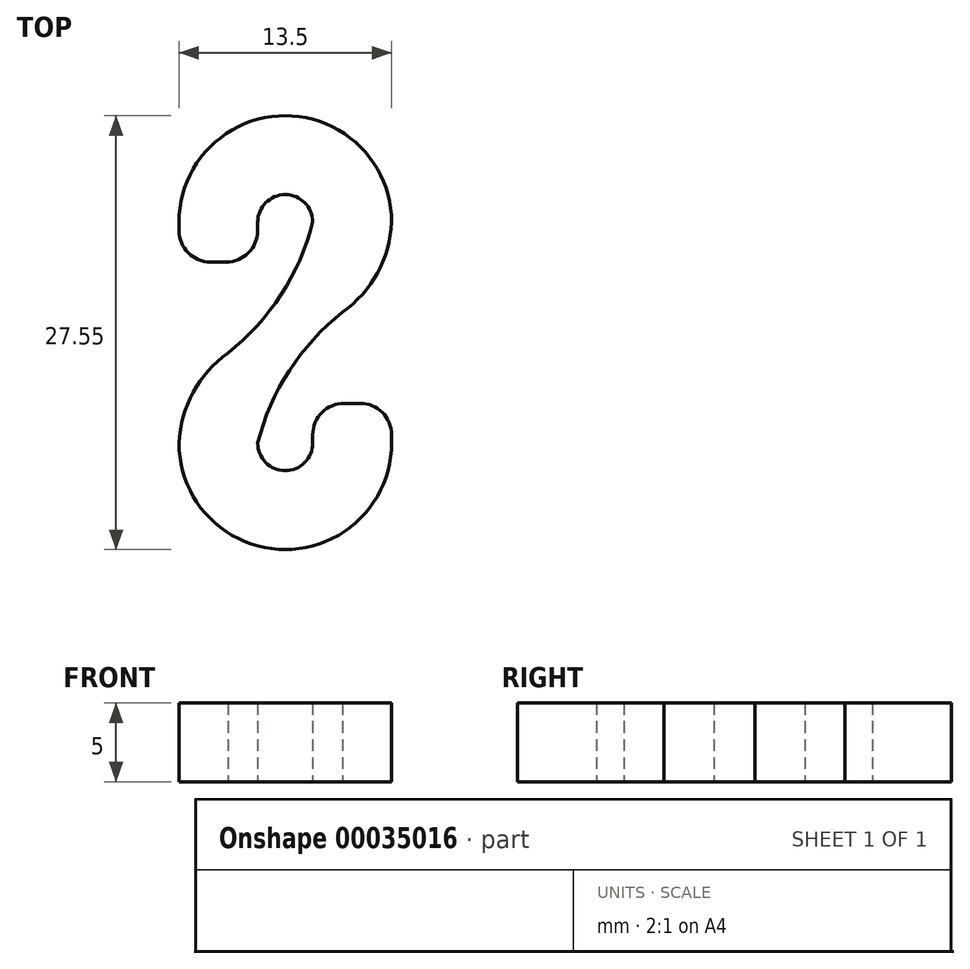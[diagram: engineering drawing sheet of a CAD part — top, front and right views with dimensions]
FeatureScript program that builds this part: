
annotation { "Feature Type Name" : "Feature", "Feature Type Description" : "" }
export const myFeature = defineFeature(function(context is Context, id is Id, definition is map)
    precondition{}
    {
        {
            var Q0;
            Q0=qCreatedBy(makeId("Top.planeOp"),FACE);
            var sketch = newSketch(context, id + "F0", { "sketchPlane" : qUnion([Q0])});
            skLineSegment(sketch, "E0", {"start": v(0, 2.86) * mm, "end": v(0, 5.23) * mm, "construction": true});
            skArc(sketch, "E1", {"start": v(6.75, 0) * mm, "mid": v(0, 6.76) * mm, "end": v(-6.75, 0) * mm});
            skLineSegment(sketch, "E2", {"start": v(3.75, -7.01) * mm, "end": v(-3.53, -7.01) * mm, "construction": true});
            skArc(sketch, "E3.MirrorCS", {"start": v(6.75, -14.03) * mm, "mid": v(0, -20.8) * mm, "end": v(-6.75, -14.03) * mm});
            skLineSegment(sketch, "E4.MirrorCS", {"start": v(0, -16.9) * mm, "end": v(0, -19.26) * mm, "construction": true});
            skArc(sketch, "E5", {"start": v(-3.64, -8.3) * mm, "mid": v(-5.85, -10.81) * mm, "end": v(-6.75, -14.03) * mm});
            skArc(sketch, "E6.MirrorCS", {"start": v(3.64, -5.72) * mm, "mid": v(5.85, -3.22) * mm, "end": v(6.75, 0) * mm});
            skArc(sketch, "E7", {"start": v(-3.64, -8.3) * mm, "mid": v(-0.26, -4.6) * mm, "end": v(1.75, 0) * mm});
            skArc(sketch, "E8.MirrorCS", {"start": v(3.64, -5.72) * mm, "mid": v(0.26, -9.43) * mm, "end": v(-1.75, -14.03) * mm});
            skArc(sketch, "E9", {"start": v(-1.75, 0) * mm, "mid": v(0, -1.75) * mm, "end": v(1.75, 0) * mm, "construction": true});
            skArc(sketch, "E10", {"start": v(1.75, 0) * mm, "mid": v(0, 1.75) * mm, "end": v(-1.75, 0) * mm});
            skArc(sketch, "E11", {"start": v(-1.75, -14.03) * mm, "mid": v(0, -12.28) * mm, "end": v(1.75, -14.03) * mm, "construction": true});
            skArc(sketch, "E12", {"start": v(1.75, -14.03) * mm, "mid": v(0, -15.78) * mm, "end": v(-1.75, -14.03) * mm});
            skLineSegment(sketch, "E13.top", {"start": v(1.75, -11.5) * mm, "end": v(6.75, -11.5) * mm});
            skLineSegment(sketch, "E13.left", {"start": v(1.75, -14.03) * mm, "end": v(1.75, -11.5) * mm});
            skLineSegment(sketch, "E13.right", {"start": v(6.75, -14.03) * mm, "end": v(6.75, -11.5) * mm});
            skLineSegment(sketch, "E14.MirrorCS", {"start": v(-1.75, 0) * mm, "end": v(-1.75, -2.53) * mm});
            skLineSegment(sketch, "E15.MirrorCS", {"start": v(-1.75, -2.53) * mm, "end": v(-6.75, -2.53) * mm});
            skLineSegment(sketch, "E16.MirrorCS", {"start": v(-6.75, 0) * mm, "end": v(-6.75, -2.53) * mm});
            skSolve(sketch);
        }
        {
            var Q0;
            Q0=makeQuery(id+"F0.imprint","IMPRINT",FACE,{"disambiguationData":[TD([[makeQuery(id+"F0.imprint","IMPRINT",EDGE,{"derivedFrom":sQuery(id+"F0.wireOp",EDGE,"E1")}),1.0]])]});
            extrude(context, id + "F1", {"entities" : qUnion([Q0]), "depth" : 5 * mm});
        }
        {
            var Q0;
            Q0=makeQuery(id+"F1.opExtrude","SWEPT_EDGE",EDGE,{"disambiguationData":[OSD([sQuery(id+"F0.wireOp",EDGE,"E15.MirrorCS"),sQuery(id+"F0.wireOp",EDGE,"E16.MirrorCS")])]});
            var Q1;
            Q1=makeQuery(id+"F1.opExtrude","SWEPT_EDGE",EDGE,{"disambiguationData":[OSD([sQuery(id+"F0.wireOp",EDGE,"E13.top"),sQuery(id+"F0.wireOp",EDGE,"E13.right")])]});
            var Q2;
            Q2=makeQuery(id+"F1.opExtrude","SWEPT_EDGE",EDGE,{"disambiguationData":[OSD([sQuery(id+"F0.wireOp",EDGE,"E13.top"),sQuery(id+"F0.wireOp",EDGE,"E13.left")])]});
            var Q3;
            Q3=makeQuery(id+"F1.opExtrude","SWEPT_EDGE",EDGE,{"disambiguationData":[OSD([sQuery(id+"F0.wireOp",EDGE,"E14.MirrorCS"),sQuery(id+"F0.wireOp",EDGE,"E15.MirrorCS")])]});
            fillet(context, id + "F2", {"entities" : qUnion([Q0, Q1, Q2, Q3]), "radius" : 2 * mm, "tangentPropagation" : true, "allowEdgeOverflow" : false});
        }
    });
